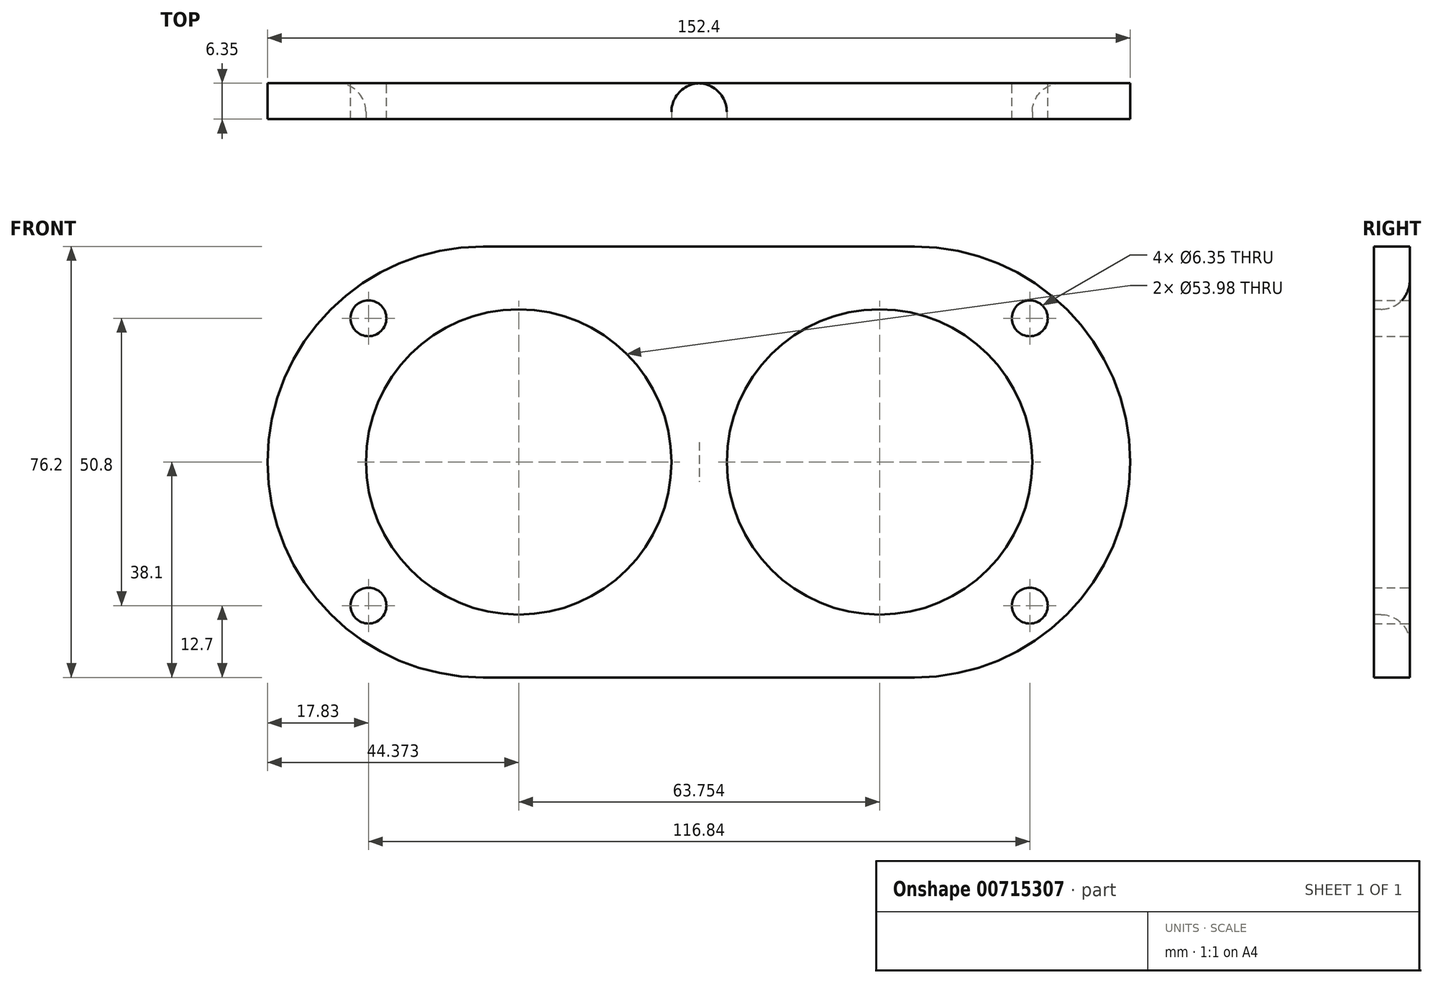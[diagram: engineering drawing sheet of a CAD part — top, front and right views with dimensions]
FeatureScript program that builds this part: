
annotation { "Feature Type Name" : "Feature", "Feature Type Description" : "" }
export const myFeature = defineFeature(function(context is Context, id is Id, definition is map)
    precondition{}
    {
        {
            var Q0;
            Q0=qCreatedBy(makeId("Front.planeOp"),FACE);
            var sketch = newSketch(context, id + "F0", { "sketchPlane" : qUnion([Q0])});
            skArc(sketch, "E0", {"start": v(-31.75, 31.75) * mm, "mid": v(-63.5, 0) * mm, "end": v(-31.75, -31.75) * mm});
            skArc(sketch, "E1", {"start": v(31.75, -31.75) * mm, "mid": v(63.5, 0) * mm, "end": v(31.75, 31.75) * mm});
            skLineSegment(sketch, "E2", {"start": v(-31.75, 31.75) * mm, "end": v(31.75, 31.75) * mm});
            skLineSegment(sketch, "E3", {"start": v(-31.75, -31.75) * mm, "end": v(31.75, -31.75) * mm});
            skCircle(sketch, "E4", {"center": v(-58.42, 25.4) * mm, "radius": 3.18 * mm});
            skCircle(sketch, "E5.MirrorC", {"center": v(58.42, 25.4) * mm, "radius": 3.18 * mm});
            skCircle(sketch, "E6.MirrorC", {"center": v(-58.42, -25.4) * mm, "radius": 3.18 * mm});
            skCircle(sketch, "E7.MirrorC", {"center": v(58.42, -25.4) * mm, "radius": 3.18 * mm});
            skLineSegment(sketch, "E8.top", {"start": v(-38.15, -38.1) * mm, "end": v(38.05, -38.1) * mm});
            skPoint(sketch, "E8.middle", {"position": v(0, 0) * mm});
            skPoint(sketch, "E9.visualSharp", {"position": v(-76.25, -38.1) * mm});
            skArc(sketch, "E9.filletArc", {"start": v(-76.25, 0) * mm, "mid": v(-65.1, -26.94) * mm, "end": v(-38.15, -38.1) * mm});
            skPoint(sketch, "E10.visualSharp", {"position": v(76.15, -38.1) * mm});
            skArc(sketch, "E10.filletArc", {"start": v(38.05, -38.1) * mm, "mid": v(64.99, -26.94) * mm, "end": v(76.15, 0) * mm});
            skLineSegment(sketch, "E11.MirrorCS", {"start": v(-38.15, 38.1) * mm, "end": v(38.05, 38.1) * mm});
            skArc(sketch, "E12.MirrorCS", {"start": v(-76.25, 0) * mm, "mid": v(-65.1, 26.94) * mm, "end": v(-38.15, 38.1) * mm});
            skArc(sketch, "E13.MirrorCS", {"start": v(38.05, 38.1) * mm, "mid": v(64.99, 26.94) * mm, "end": v(76.15, 0) * mm});
            skSolve(sketch);
        }
        {
            var Q0;
            Q0=qSketchRegion(id+"F0",true);
            extrude(context, id + "F1", {"entities" : qUnion([Q0]), "depth" : 6.35 * mm, "offsetDistance" : 25.4 * mm});
        }
        {
            var Q0;
            Q0=makeQuery(id+"F0.imprint","IMPRINT",FACE,{"disambiguationData":[TD([[makeQuery(id+"F0.imprint","IMPRINT",EDGE,{"derivedFrom":sQuery(id+"F0.wireOp",EDGE,"E0")}),1.0]])]});
            extrude(context, id + "F2", {"entities" : qUnion([Q0]), "operationType" : NewBodyOperationType.ADD, "depth" : 6.35 * mm, "offsetDistance" : 25.4 * mm});
        }
        {
            var Q0;
            {var subQ0=sQuery(id+"F0.wireOp",EDGE,"E3");var subQ1=sQuery(id+"F0.wireOp",EDGE,"E2");var subQ2=sQuery(id+"F0.wireOp",EDGE,"E1");var subQ3=sQuery(id+"F0.wireOp",EDGE,"E0");Q0=makeQuery(id+"F2.boolean.opBoolean","MERGE",FACE,{"derivedFrom":[makeQuery(id+"F1.opExtrude","CAP_FACE",FACE,{"disambiguationData":[OSD([subQ3,subQ2,subQ1,subQ0,sQuery(id+"F0.wireOp",EDGE,"E4"),sQuery(id+"F0.wireOp",EDGE,"E5.MirrorC"),sQuery(id+"F0.wireOp",EDGE,"E6.MirrorC"),sQuery(id+"F0.wireOp",EDGE,"E7.MirrorC"),sQuery(id+"F0.wireOp",EDGE,"E8.top"),sQuery(id+"F0.wireOp",EDGE,"E9.filletArc"),sQuery(id+"F0.wireOp",EDGE,"E10.filletArc"),sQuery(id+"F0.wireOp",EDGE,"E11.MirrorCS"),sQuery(id+"F0.wireOp",EDGE,"E12.MirrorCS"),sQuery(id+"F0.wireOp",EDGE,"E13.MirrorCS")])],"isStart":false}),makeQuery(id+"F2.opExtrude","CAP_FACE",FACE,{"disambiguationData":[OSD([subQ3,subQ2,subQ1,subQ0])],"isStart":false})]});}
            var sketch = newSketch(context, id + "F3", { "sketchPlane" : qUnion([Q0])});
            skCircle(sketch, "E14", {"center": v(31.75, 0) * mm, "radius": 31.5 * mm});
            skCircle(sketch, "E15", {"center": v(-31.75, 0) * mm, "radius": 31.5 * mm});
            skSolve(sketch);
        }
        {
            var Q0;
            Q0=makeQuery(id+"F3.imprint","IMPRINT",FACE,{"disambiguationData":[TD([[makeQuery(id+"F3.imprint","IMPRINT",EDGE,{"derivedFrom":sQuery(id+"F3.wireOp",EDGE,"E14")}),-1.0]])]});
            var sketch = newSketch(context, id + "F4", { "sketchPlane" : qUnion([Q0])});
            skCircle(sketch, "E16", {"center": v(31.88, 0) * mm, "radius": 26.99 * mm});
            skCircle(sketch, "E17", {"center": v(-31.88, 0) * mm, "radius": 26.99 * mm});
            skSolve(sketch);
        }
        {
            var Q0;
            Q0=makeQuery(id+"F4.imprint","IMPRINT",FACE,{"disambiguationData":[TD([[makeQuery(id+"F4.imprint","IMPRINT",EDGE,{"derivedFrom":sQuery(id+"F4.wireOp",EDGE,"E17")}),1.0]])]});
            var Q1;
            Q1=makeQuery(id+"F4.imprint","IMPRINT",FACE,{"disambiguationData":[TD([[makeQuery(id+"F4.imprint","IMPRINT",EDGE,{"derivedFrom":sQuery(id+"F4.wireOp",EDGE,"E16")}),1.0]])]});
            extrude(context, id + "F5", {"entities" : qUnion([Q0, Q1]), "operationType" : NewBodyOperationType.REMOVE, "oppositeDirection" : true, "depth" : 25.4 * mm, "offsetDistance" : 25.4 * mm});
        }
        {
            var Q0;
            {var subQ0=sQuery(id+"F0.wireOp",EDGE,"E3");var subQ1=sQuery(id+"F0.wireOp",EDGE,"E2");var subQ2=sQuery(id+"F0.wireOp",EDGE,"E1");var subQ3=sQuery(id+"F0.wireOp",EDGE,"E0");Q0=makeQuery(id+"F5.boolean.opBoolean","INTERSECT",EDGE,{"derivedFrom":[makeQuery(id+"F2.boolean.opBoolean","MERGE",FACE,{"derivedFrom":[makeQuery(id+"F1.opExtrude","CAP_FACE",FACE,{"disambiguationData":[OSD([subQ3,subQ2,subQ1,subQ0,sQuery(id+"F0.wireOp",EDGE,"E4"),sQuery(id+"F0.wireOp",EDGE,"E5.MirrorC"),sQuery(id+"F0.wireOp",EDGE,"E6.MirrorC"),sQuery(id+"F0.wireOp",EDGE,"E7.MirrorC"),sQuery(id+"F0.wireOp",EDGE,"E8.top"),sQuery(id+"F0.wireOp",EDGE,"E9.filletArc"),sQuery(id+"F0.wireOp",EDGE,"E10.filletArc"),sQuery(id+"F0.wireOp",EDGE,"E11.MirrorCS"),sQuery(id+"F0.wireOp",EDGE,"E12.MirrorCS"),sQuery(id+"F0.wireOp",EDGE,"E13.MirrorCS")])],"isStart":true}),makeQuery(id+"F2.opExtrude","CAP_FACE",FACE,{"disambiguationData":[OSD([subQ3,subQ2,subQ1,subQ0])],"isStart":true})]}),makeQuery(id+"F5.opExtrude","SWEPT_FACE",FACE,{"disambiguationData":[OSD([sQuery(id+"F4.wireOp",EDGE,"E16")])]})]});}
            var Q1;
            {var subQ0=sQuery(id+"F0.wireOp",EDGE,"E3");var subQ1=sQuery(id+"F0.wireOp",EDGE,"E2");var subQ2=sQuery(id+"F0.wireOp",EDGE,"E1");var subQ3=sQuery(id+"F0.wireOp",EDGE,"E0");Q1=makeQuery(id+"F5.boolean.opBoolean","INTERSECT",EDGE,{"derivedFrom":[makeQuery(id+"F2.boolean.opBoolean","MERGE",FACE,{"derivedFrom":[makeQuery(id+"F1.opExtrude","CAP_FACE",FACE,{"disambiguationData":[OSD([subQ3,subQ2,subQ1,subQ0,sQuery(id+"F0.wireOp",EDGE,"E4"),sQuery(id+"F0.wireOp",EDGE,"E5.MirrorC"),sQuery(id+"F0.wireOp",EDGE,"E6.MirrorC"),sQuery(id+"F0.wireOp",EDGE,"E7.MirrorC"),sQuery(id+"F0.wireOp",EDGE,"E8.top"),sQuery(id+"F0.wireOp",EDGE,"E9.filletArc"),sQuery(id+"F0.wireOp",EDGE,"E10.filletArc"),sQuery(id+"F0.wireOp",EDGE,"E11.MirrorCS"),sQuery(id+"F0.wireOp",EDGE,"E12.MirrorCS"),sQuery(id+"F0.wireOp",EDGE,"E13.MirrorCS")])],"isStart":true}),makeQuery(id+"F2.opExtrude","CAP_FACE",FACE,{"disambiguationData":[OSD([subQ3,subQ2,subQ1,subQ0])],"isStart":true})]}),makeQuery(id+"F5.opExtrude","SWEPT_FACE",FACE,{"disambiguationData":[OSD([sQuery(id+"F4.wireOp",EDGE,"E17")])]})]});}
            fillet(context, id + "F6", {"entities" : qUnion([Q0, Q1]), "radius" : 5.08 * mm, "tangentPropagation" : true, "allowEdgeOverflow" : false});
        }
    });
